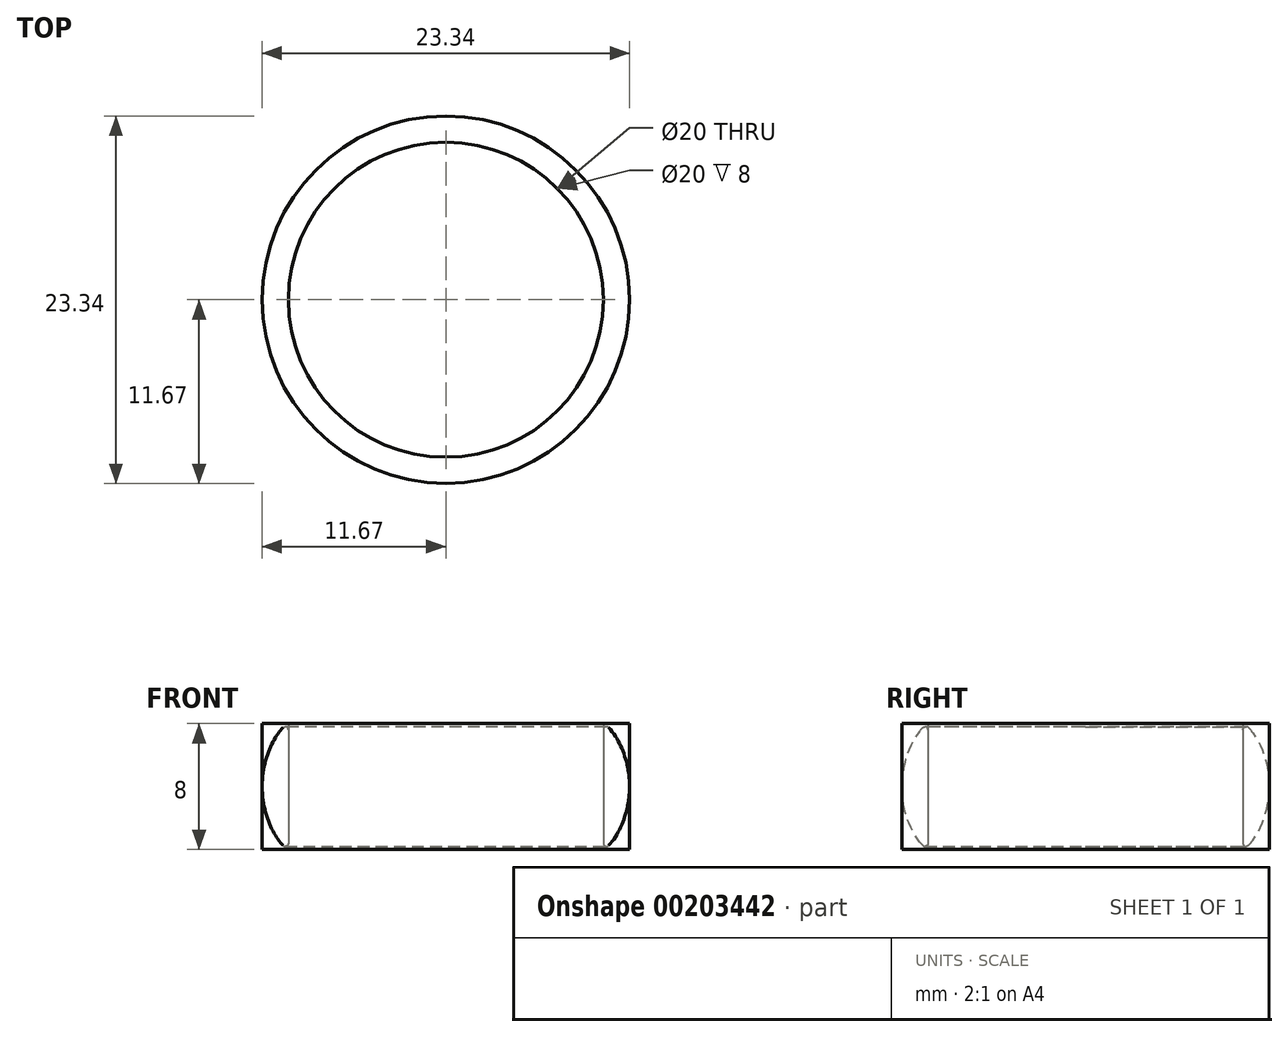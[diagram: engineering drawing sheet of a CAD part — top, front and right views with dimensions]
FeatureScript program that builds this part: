
annotation { "Feature Type Name" : "Feature", "Feature Type Description" : "" }
export const myFeature = defineFeature(function(context is Context, id is Id, definition is map)
    precondition{}
    {
        {
            var Q0;
            Q0=qCreatedBy(makeId("Top.planeOp"),FACE);
            var sketch = newSketch(context, id + "F0", { "sketchPlane" : qUnion([Q0])});
            skCircle(sketch, "E0", {"center": v(0, 0) * mm, "radius": 10 * mm});
            skCircle(sketch, "E1", {"center": v(0, 0) * mm, "radius": 11.67 * mm});
            skPoint(sketch, "E2", {"position": v(11.67, 0) * mm});
            skSolve(sketch);
        }
        {
            var Q0;
            Q0=makeQuery(id+"F0.imprint","IMPRINT",FACE,{"disambiguationData":[TD([[makeQuery(id+"F0.imprint","IMPRINT",EDGE,{"derivedFrom":sQuery(id+"F0.wireOp",EDGE,"E0")}),-1.0]])]});
            extrude(context, id + "F1", {"entities" : qUnion([Q0]), "depth" : 8 * mm});
        }
        {
            var Q0;
            Q0=qCreatedBy(makeId("Front.planeOp"),FACE);
            var sketch = newSketch(context, id + "F2", { "sketchPlane" : qUnion([Q0])});
            skLineSegment(sketch, "E3.0", {"start": v(-10, 8) * mm, "end": v(10, 8) * mm, "construction": true});
            skLineSegment(sketch, "E4.0", {"start": v(-10, 0) * mm, "end": v(10, 0) * mm, "construction": true});
            skLineSegment(sketch, "E5.0", {"start": v(-11.67, 0) * mm, "end": v(11.67, 0) * mm, "construction": true});
            skLineSegment(sketch, "E6.0", {"start": v(-11.67, 8) * mm, "end": v(11.67, 8) * mm, "construction": true});
            skLineSegment(sketch, "E7", {"start": v(11.67, 8) * mm, "end": v(11.67, 0) * mm, "construction": true});
            skPoint(sketch, "E8", {"position": v(11.67, 4) * mm});
            skFitSpline(sketch, "E9", {"points": [v(10, 8) * mm, v(11.67, 4) * mm], "startDerivative": vector(1.94, -0.95) * mm, "endDerivative": vector(0, -6.12) * mm});
            skLineSegment(sketch, "E10", {"start": v(11.67, 4) * mm, "end": v(-11.67, 4) * mm, "construction": true});
            skFitSpline(sketch, "E11.MirrorCS", {"points": [v(10, 0) * mm, v(11.67, 4) * mm], "startDerivative": vector(1.94, 0.95) * mm, "endDerivative": vector(0, 6.12) * mm});
            skLineSegment(sketch, "E12", {"start": v(10, 8) * mm, "end": v(10, 0) * mm});
            skLineSegment(sketch, "E13", {"start": v(0, 0) * mm, "end": v(0, 8) * mm, "construction": true});
            skSolve(sketch);
        }
        {
            var Q0;
            Q0=makeQuery(id+"F2.imprint","IMPRINT",FACE,{"disambiguationData":[TD([[makeQuery(id+"F2.imprint","IMPRINT",EDGE,{"derivedFrom":sQuery(id+"F2.wireOp",EDGE,"E9")}),-1.0]])]});
            var Q1;
            Q1=sQuery(id+"F2.wireOp",EDGE,"E13");
            revolve(context, id + "F3", {"entities" : qUnion([Q0]), "axis" : qUnion([Q1]), "revolveType" : RevolveType.FULL});
        }
        {
            var Q0;
            Q0=makeQuery(id+"F3.opRevolve","SWEPT_EDGE",EDGE,{"disambiguationData":[OSD([sQuery(id+"F2.wireOp",EDGE,"E11.MirrorCS"),sQuery(id+"F2.wireOp",EDGE,"E12")])]});
            var Q1;
            Q1=makeQuery(id+"F3.opRevolve","SWEPT_EDGE",EDGE,{"disambiguationData":[OSD([sQuery(id+"F2.wireOp",EDGE,"E9"),sQuery(id+"F2.wireOp",EDGE,"E12")])]});
            fillet(context, id + "F4", {"entities" : qUnion([Q0, Q1]), "radius" : 0.2 * mm, "tangentPropagation" : true, "allowEdgeOverflow" : false});
        }
    });
